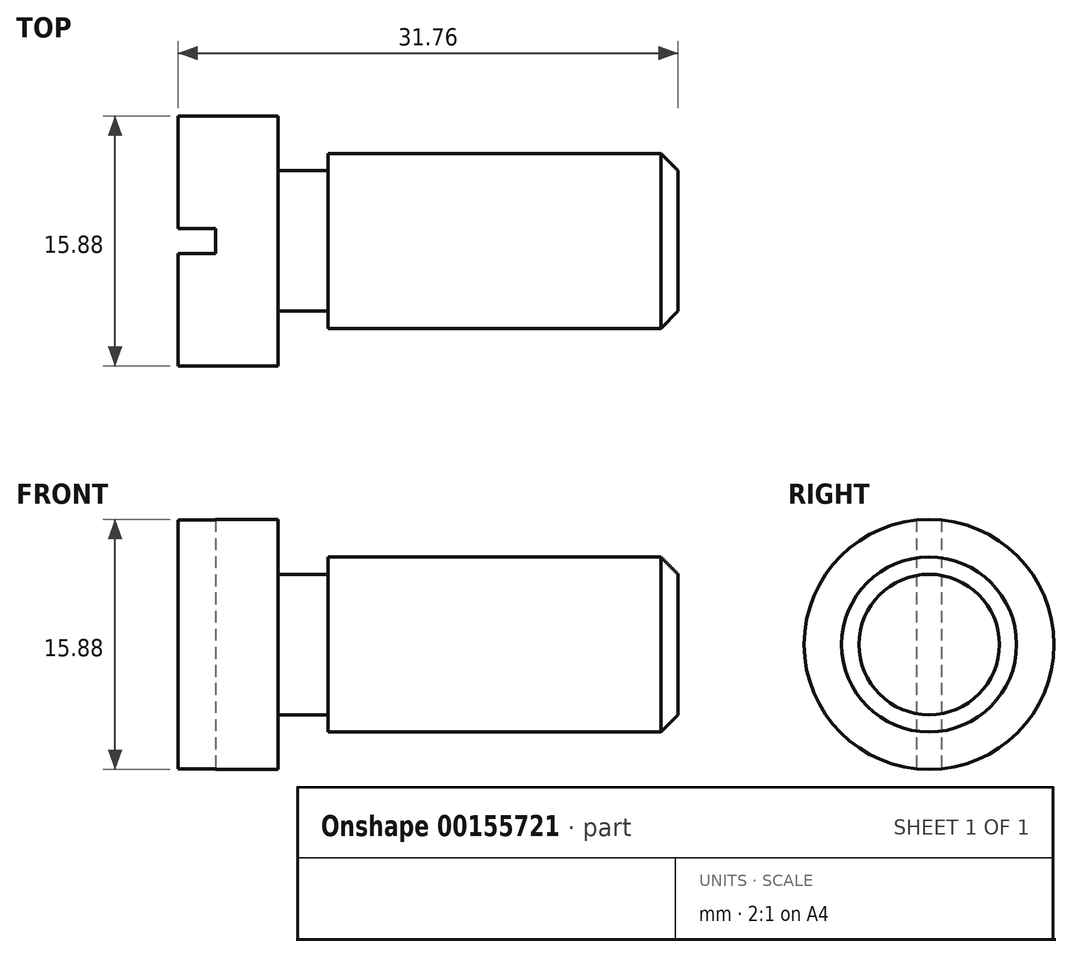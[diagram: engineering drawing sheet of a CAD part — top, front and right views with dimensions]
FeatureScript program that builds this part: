
annotation { "Feature Type Name" : "Feature", "Feature Type Description" : "" }
export const myFeature = defineFeature(function(context is Context, id is Id, definition is map)
    precondition{}
    {
        {
            var Q0;
            Q0=qCreatedBy(makeId("Front.planeOp"),FACE);
            var sketch = newSketch(context, id + "F0", { "sketchPlane" : qUnion([Q0])});
            skLineSegment(sketch, "E0.bottom", {"start": v(-15.88, 7.94) * mm, "end": v(-9.53, 7.94) * mm});
            skLineSegment(sketch, "E0.top", {"start": v(-15.88, 0) * mm, "end": v(15.88, 0) * mm});
            skLineSegment(sketch, "E0.left", {"start": v(-15.88, 7.94) * mm, "end": v(-15.88, 0) * mm});
            skLineSegment(sketch, "E0.right", {"start": v(15.88, 4.46) * mm, "end": v(15.88, 0) * mm});
            skLineSegment(sketch, "E1", {"start": v(-9.53, 7.94) * mm, "end": v(-9.53, 4.46) * mm});
            skLineSegment(sketch, "E2", {"start": v(-6.35, 5.56) * mm, "end": v(14.78, 5.56) * mm});
            skLineSegment(sketch, "E3", {"start": v(15.87, 4.46) * mm, "end": v(14.78, 5.56) * mm});
            skLineSegment(sketch, "E4", {"start": v(-6.35, 5.56) * mm, "end": v(-6.35, 4.46) * mm});
            skLineSegment(sketch, "E5", {"start": v(-6.35, 4.46) * mm, "end": v(-9.52, 4.46) * mm});
            skSolve(sketch);
        }
        {
            var Q0;
            Q0 = qSketchRegion(id + "F0", true);
            var Q1;
            Q1=sQuery(id+"F0.wireOp",EDGE,"E0.top");
            revolve(context, id + "F1", {"entities" : qUnion([Q0]), "axis" : qUnion([Q1]), "revolveType" : RevolveType.FULL});
        }
        {
            var Q0;
            Q0=makeQuery(id+"F1.opRevolve","SWEPT_FACE",FACE,{"disambiguationData":[OSD([sQuery(id+"F0.wireOp",EDGE,"E0.left")])]});
            var sketch = newSketch(context, id + "F3", { "sketchPlane" : qUnion([Q0])});
            skLineSegment(sketch, "E6.bottom", {"start": v(-0.8, 7.94) * mm, "end": v(0.8, 7.94) * mm});
            skLineSegment(sketch, "E6.top", {"start": v(-0.8, -7.94) * mm, "end": v(0.8, -7.94) * mm});
            skLineSegment(sketch, "E6.left", {"start": v(-0.8, 7.94) * mm, "end": v(-0.8, -7.94) * mm});
            skLineSegment(sketch, "E6.right", {"start": v(0.8, 7.94) * mm, "end": v(0.8, -7.94) * mm});
            skPoint(sketch, "E6.middle", {"position": v(0, 0) * mm});
            skSolve(sketch);
        }
        {
            var Q0;
            Q0 = qSketchRegion(id + "F3", true);
            extrude(context, id + "F2", {"entities" : qUnion([Q0]), "operationType" : NewBodyOperationType.REMOVE, "oppositeDirection" : true, "depth" : 2.38 * mm});
        }
    });
